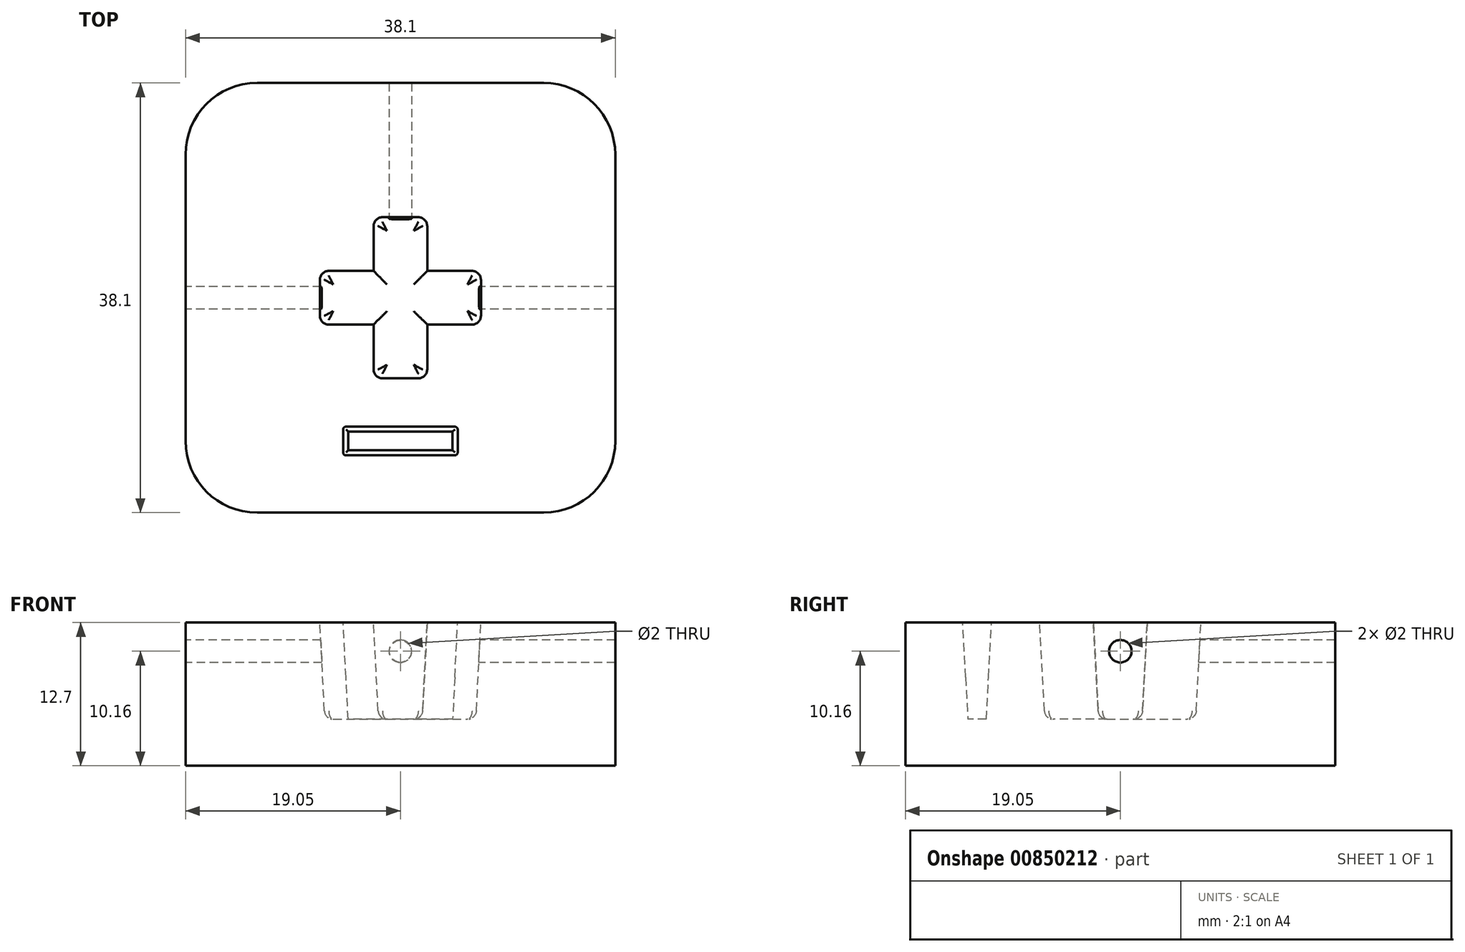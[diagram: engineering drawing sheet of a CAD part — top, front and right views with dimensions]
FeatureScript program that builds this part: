
annotation { "Feature Type Name" : "Feature", "Feature Type Description" : "" }
export const myFeature = defineFeature(function(context is Context, id is Id, definition is map)
    precondition{}
    {
        {
            var Q0;
            Q0=qCreatedBy(makeId("Top.planeOp"),FACE);
            var sketch = newSketch(context, id + "F0", { "sketchPlane" : qUnion([Q0])});
            skLineSegment(sketch, "E0.bottom", {"start": v(12.7, 19.05) * mm, "end": v(-12.7, 19.05) * mm});
            skLineSegment(sketch, "E0.top", {"start": v(12.7, -19.05) * mm, "end": v(-12.7, -19.05) * mm});
            skLineSegment(sketch, "E0.left", {"start": v(19.05, 12.7) * mm, "end": v(19.05, -12.7) * mm});
            skLineSegment(sketch, "E0.right", {"start": v(-19.05, 12.7) * mm, "end": v(-19.05, -12.7) * mm});
            skPoint(sketch, "E0.middle", {"position": v(0, 0) * mm});
            skPoint(sketch, "E1.visualSharp", {"position": v(-19.05, 19.05) * mm});
            skArc(sketch, "E1.filletArc", {"start": v(-12.7, 19.05) * mm, "mid": v(-17.2, 17.2) * mm, "end": v(-19.05, 12.7) * mm});
            skPoint(sketch, "E2.visualSharp", {"position": v(19.05, 19.05) * mm});
            skArc(sketch, "E2.filletArc", {"start": v(19.05, 12.7) * mm, "mid": v(17.2, 17.2) * mm, "end": v(12.7, 19.05) * mm});
            skPoint(sketch, "E3.visualSharp", {"position": v(19.05, -19.05) * mm});
            skArc(sketch, "E3.filletArc", {"start": v(12.7, -19.05) * mm, "mid": v(17.2, -17.2) * mm, "end": v(19.05, -12.7) * mm});
            skPoint(sketch, "E4.visualSharp", {"position": v(-19.05, -19.05) * mm});
            skArc(sketch, "E4.filletArc", {"start": v(-19.05, -12.7) * mm, "mid": v(-17.2, -17.2) * mm, "end": v(-12.7, -19.05) * mm});
            skSolve(sketch);
        }
        {
            var Q0;
            Q0=qCreatedBy(makeId("Top.planeOp"),FACE);
            var sketch = newSketch(context, id + "F1", { "sketchPlane" : qUnion([Q0])});
            skLineSegment(sketch, "E5.bottom", {"start": v(1.59, 7.14) * mm, "end": v(-1.59, 7.14) * mm});
            skLineSegment(sketch, "E5.top", {"start": v(1.59, -7.14) * mm, "end": v(-1.59, -7.14) * mm});
            skLineSegment(sketch, "E5.left", {"start": v(2.38, 6.35) * mm, "end": v(2.38, 2.38) * mm});
            skLineSegment(sketch, "E5.right", {"start": v(-2.38, 6.35) * mm, "end": v(-2.38, 2.38) * mm});
            skPoint(sketch, "E5.middle", {"position": v(0, 0) * mm});
            skLineSegment(sketch, "E6.bottom", {"start": v(6.35, 2.38) * mm, "end": v(2.38, 2.38) * mm});
            skLineSegment(sketch, "E6.top", {"start": v(6.35, -2.38) * mm, "end": v(2.38, -2.38) * mm});
            skLineSegment(sketch, "E6.left", {"start": v(7.14, 1.59) * mm, "end": v(7.14, -1.59) * mm});
            skLineSegment(sketch, "E6.right", {"start": v(-7.14, 1.59) * mm, "end": v(-7.14, -1.59) * mm});
            skPoint(sketch, "E7.visualSharp", {"position": v(-2.38, 7.14) * mm});
            skArc(sketch, "E7.filletArc", {"start": v(-1.59, 7.14) * mm, "mid": v(-2.15, 6.91) * mm, "end": v(-2.38, 6.35) * mm});
            skPoint(sketch, "E8.visualSharp", {"position": v(2.38, 7.14) * mm});
            skArc(sketch, "E8.filletArc", {"start": v(2.38, 6.35) * mm, "mid": v(2.15, 6.91) * mm, "end": v(1.59, 7.14) * mm});
            skPoint(sketch, "E9.visualSharp", {"position": v(7.14, 2.38) * mm});
            skArc(sketch, "E9.filletArc", {"start": v(7.14, 1.59) * mm, "mid": v(6.91, 2.15) * mm, "end": v(6.35, 2.38) * mm});
            skPoint(sketch, "E10.visualSharp", {"position": v(7.14, -2.38) * mm});
            skArc(sketch, "E10.filletArc", {"start": v(6.35, -2.38) * mm, "mid": v(6.91, -2.15) * mm, "end": v(7.14, -1.59) * mm});
            skPoint(sketch, "E11.visualSharp", {"position": v(2.38, -7.14) * mm});
            skArc(sketch, "E11.filletArc", {"start": v(1.59, -7.14) * mm, "mid": v(2.15, -6.91) * mm, "end": v(2.38, -6.35) * mm});
            skPoint(sketch, "E12.visualSharp", {"position": v(-2.38, -7.14) * mm});
            skArc(sketch, "E12.filletArc", {"start": v(-2.38, -6.35) * mm, "mid": v(-2.15, -6.91) * mm, "end": v(-1.59, -7.14) * mm});
            skPoint(sketch, "E13.visualSharp", {"position": v(-7.14, -2.38) * mm});
            skArc(sketch, "E13.filletArc", {"start": v(-7.14, -1.59) * mm, "mid": v(-6.91, -2.15) * mm, "end": v(-6.35, -2.38) * mm});
            skPoint(sketch, "E14.visualSharp", {"position": v(-7.14, 2.38) * mm});
            skArc(sketch, "E14.filletArc", {"start": v(-6.35, 2.38) * mm, "mid": v(-6.91, 2.15) * mm, "end": v(-7.14, 1.59) * mm});
            skLineSegment(sketch, "E15.trimOffspring", {"start": v(-2.38, 2.38) * mm, "end": v(-6.35, 2.38) * mm});
            skLineSegment(sketch, "E16.trimOffspring", {"start": v(-2.38, -2.38) * mm, "end": v(-2.38, -6.35) * mm});
            skLineSegment(sketch, "E17.trimOffspring", {"start": v(2.38, -2.38) * mm, "end": v(2.38, -6.35) * mm});
            skLineSegment(sketch, "E18.trimOffspring", {"start": v(-2.38, -2.38) * mm, "end": v(-6.35, -2.38) * mm});
            skLineSegment(sketch, "E19", {"start": v(0, 0) * mm, "end": v(0, -12.7) * mm, "construction": true});
            skPoint(sketch, "E19.endSnap0", {"position": v(0, -7.14) * mm});
            skLineSegment(sketch, "E20.bottom", {"start": v(4.83, -11.43) * mm, "end": v(-4.83, -11.43) * mm});
            skLineSegment(sketch, "E20.top", {"start": v(4.83, -13.97) * mm, "end": v(-4.83, -13.97) * mm});
            skLineSegment(sketch, "E20.left", {"start": v(5.08, -11.68) * mm, "end": v(5.08, -13.72) * mm});
            skLineSegment(sketch, "E20.right", {"start": v(-5.08, -11.68) * mm, "end": v(-5.08, -13.72) * mm});
            skPoint(sketch, "E20.middle", {"position": v(0, -12.7) * mm});
            skPoint(sketch, "E21.visualSharp", {"position": v(-5.08, -13.97) * mm});
            skArc(sketch, "E21.filletArc", {"start": v(-5.08, -13.72) * mm, "mid": v(-5, -13.9) * mm, "end": v(-4.83, -13.97) * mm});
            skPoint(sketch, "E22.visualSharp", {"position": v(-5.08, -11.43) * mm});
            skArc(sketch, "E22.filletArc", {"start": v(-4.83, -11.43) * mm, "mid": v(-5, -11.5) * mm, "end": v(-5.08, -11.68) * mm});
            skPoint(sketch, "E23.visualSharp", {"position": v(5.08, -11.43) * mm});
            skArc(sketch, "E23.filletArc", {"start": v(5.08, -11.68) * mm, "mid": v(5, -11.5) * mm, "end": v(4.83, -11.43) * mm});
            skPoint(sketch, "E24.visualSharp", {"position": v(5.08, -13.97) * mm});
            skArc(sketch, "E24.filletArc", {"start": v(4.83, -13.97) * mm, "mid": v(5, -13.9) * mm, "end": v(5.08, -13.72) * mm});
            skSolve(sketch);
        }
        {
            var Q0;
            Q0 = qSketchRegion(id + "F0", true);
            extrude(context, id + "F2", {"entities" : qUnion([Q0]), "oppositeDirection" : true, "depth" : 12.7 * mm, "offsetDistance" : 25.4 * mm});
        }
        {
            var Q0;
            Q0 = qSketchRegion(id + "F1", true);
            extrude(context, id + "F3", {"entities" : qUnion([Q0]), "operationType" : NewBodyOperationType.REMOVE, "oppositeDirection" : true, "depth" : 8.57 * mm, "offsetDistance" : 25.4 * mm, "hasDraft" : true, "draftAngle" : 3 * degree, "draftPullDirection" : true});
        }
        {
            var Q0;
            Q0=makeQuery(id+"F3.boolean.opBoolean","COPY",FACE,{"derivedFrom":makeQuery(id+"F3.opExtrude","CAP_FACE",FACE,{"disambiguationData":[OSD([sQuery(id+"F1.wireOp",EDGE,"E5.bottom"),sQuery(id+"F1.wireOp",EDGE,"E5.top"),sQuery(id+"F1.wireOp",EDGE,"E5.left"),sQuery(id+"F1.wireOp",EDGE,"E5.right"),sQuery(id+"F1.wireOp",EDGE,"E6.bottom"),sQuery(id+"F1.wireOp",EDGE,"E6.top"),sQuery(id+"F1.wireOp",EDGE,"E6.left"),sQuery(id+"F1.wireOp",EDGE,"E6.right"),sQuery(id+"F1.wireOp",EDGE,"E7.filletArc"),sQuery(id+"F1.wireOp",EDGE,"E8.filletArc"),sQuery(id+"F1.wireOp",EDGE,"E9.filletArc"),sQuery(id+"F1.wireOp",EDGE,"E10.filletArc"),sQuery(id+"F1.wireOp",EDGE,"E11.filletArc"),sQuery(id+"F1.wireOp",EDGE,"E12.filletArc"),sQuery(id+"F1.wireOp",EDGE,"E13.filletArc"),sQuery(id+"F1.wireOp",EDGE,"E14.filletArc"),sQuery(id+"F1.wireOp",EDGE,"E15.trimOffspring"),sQuery(id+"F1.wireOp",EDGE,"E16.trimOffspring"),sQuery(id+"F1.wireOp",EDGE,"E17.trimOffspring"),sQuery(id+"F1.wireOp",EDGE,"E18.trimOffspring")])],"isStart":false})});
            fillet(context, id + "F4", {"entities" : qUnion([Q0]), "tangentPropagation" : true, "radius" : 0.8 * mm, "defaultsChanged" : true, "vertexSettings" : [], "allowEdgeOverflow" : false});
        }
        {
            var Q0;
            Q0=qCreatedBy(makeId("Front.planeOp"),FACE);
            var sketch = newSketch(context, id + "F5", { "sketchPlane" : qUnion([Q0])});
            skLineSegment(sketch, "E25", {"start": v(0, 0) * mm, "end": v(0, -2.54) * mm, "construction": true});
            skCircle(sketch, "E26", {"center": v(0, -2.54) * mm, "radius": 1 * mm});
            skSolve(sketch);
        }
        {
            var Q0;
            Q0 = qSketchRegion(id + "F5", true);
            extrude(context, id + "F6", {"entities" : qUnion([Q0]), "operationType" : NewBodyOperationType.REMOVE, "endBound" : BoundingType.THROUGH_ALL, "oppositeDirection" : true, "depth" : 25.4 * mm, "offsetDistance" : 25.4 * mm});
        }
        {
            var Q0;
            Q0=qCreatedBy(makeId("Right.planeOp"),FACE);
            var sketch = newSketch(context, id + "F7", { "sketchPlane" : qUnion([Q0])});
            skLineSegment(sketch, "E27", {"start": v(0, 0) * mm, "end": v(0, -2.54) * mm, "construction": true});
            skCircle(sketch, "E28", {"center": v(0, -2.54) * mm, "radius": 1 * mm});
            skSolve(sketch);
        }
        {
            var Q0;
            Q0 = qSketchRegion(id + "F7", true);
            extrude(context, id + "F8", {"entities" : qUnion([Q0]), "operationType" : NewBodyOperationType.REMOVE, "endBound" : BoundingType.THROUGH_ALL, "depth" : 25.4 * mm, "offsetDistance" : 25.4 * mm, "hasSecondDirection" : true, "secondDirectionBound" : SecondDirectionBoundingType.THROUGH_ALL, "secondDirectionOppositeDirection" : true, "secondDirectionDepth" : 25.4 * mm});
        }
    });
